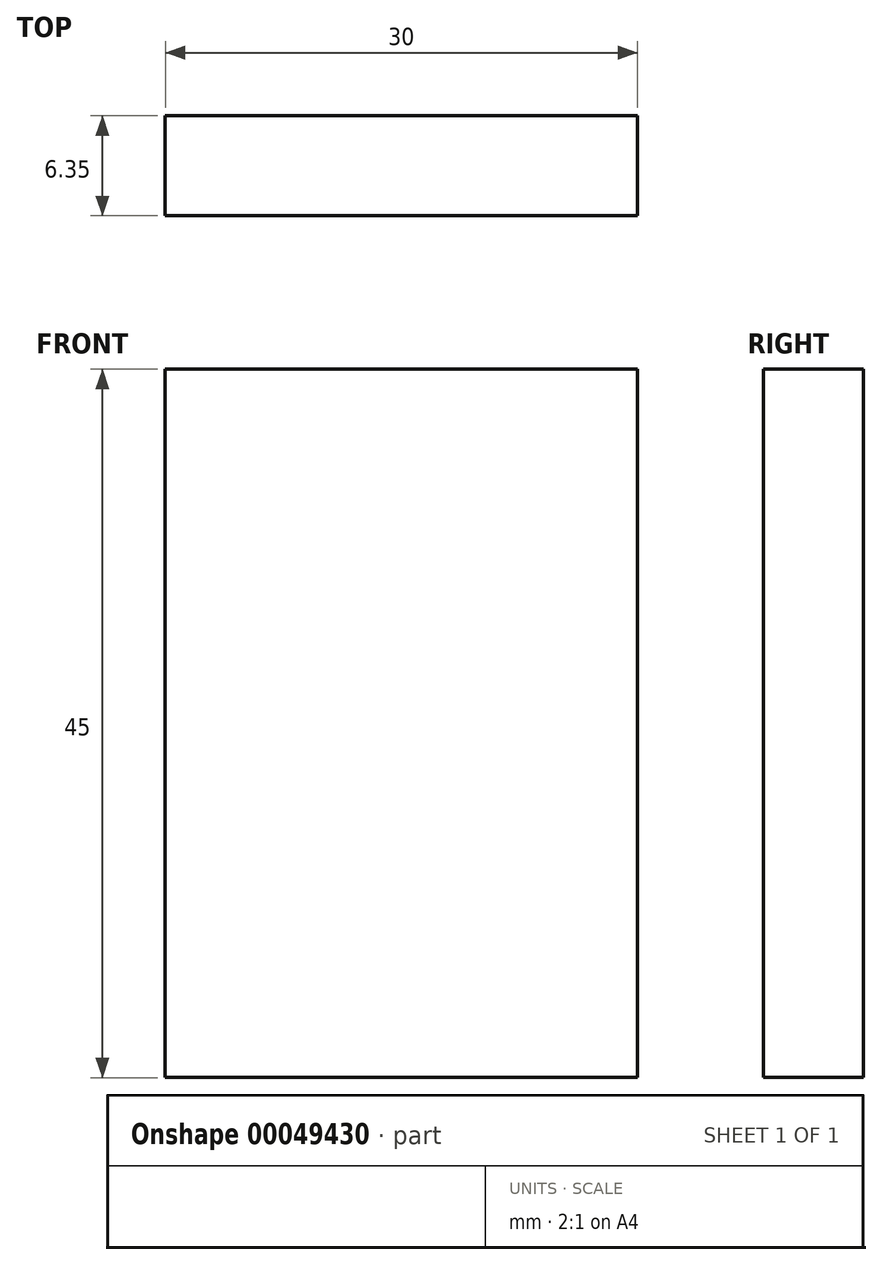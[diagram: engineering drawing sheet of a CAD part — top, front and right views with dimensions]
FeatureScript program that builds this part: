
annotation { "Feature Type Name" : "Feature", "Feature Type Description" : "" }
export const myFeature = defineFeature(function(context is Context, id is Id, definition is map)
    precondition{}
    {
        {
            var Q0;
            Q0=qCreatedBy(makeId("Front.planeOp"),FACE);
            var sketch = newSketch(context, id + "F0", { "sketchPlane" : qUnion([Q0])});
            skLineSegment(sketch, "E0.bottom", {"start": v(-14.42, 48.6) * mm, "end": v(15.58, 48.6) * mm});
            skLineSegment(sketch, "E0.top", {"start": v(-14.42, 3.6) * mm, "end": v(15.58, 3.6) * mm});
            skLineSegment(sketch, "E0.left", {"start": v(-14.42, 48.6) * mm, "end": v(-14.42, 3.6) * mm});
            skLineSegment(sketch, "E0.right", {"start": v(15.58, 48.6) * mm, "end": v(15.58, 3.6) * mm});
            skSolve(sketch);
        }
        {
            var Q0;
            Q0=makeQuery(id+"F0.imprint","IMPRINT",FACE,{"disambiguationData":[TD([[makeQuery(id+"F0.imprint","IMPRINT",EDGE,{"derivedFrom":sQuery(id+"F0.wireOp",EDGE,"E0.bottom")}),-1.0]])]});
            extrude(context, id + "F1", {"entities" : qUnion([Q0]), "depth" : 6.35 * mm});
        }
    });
